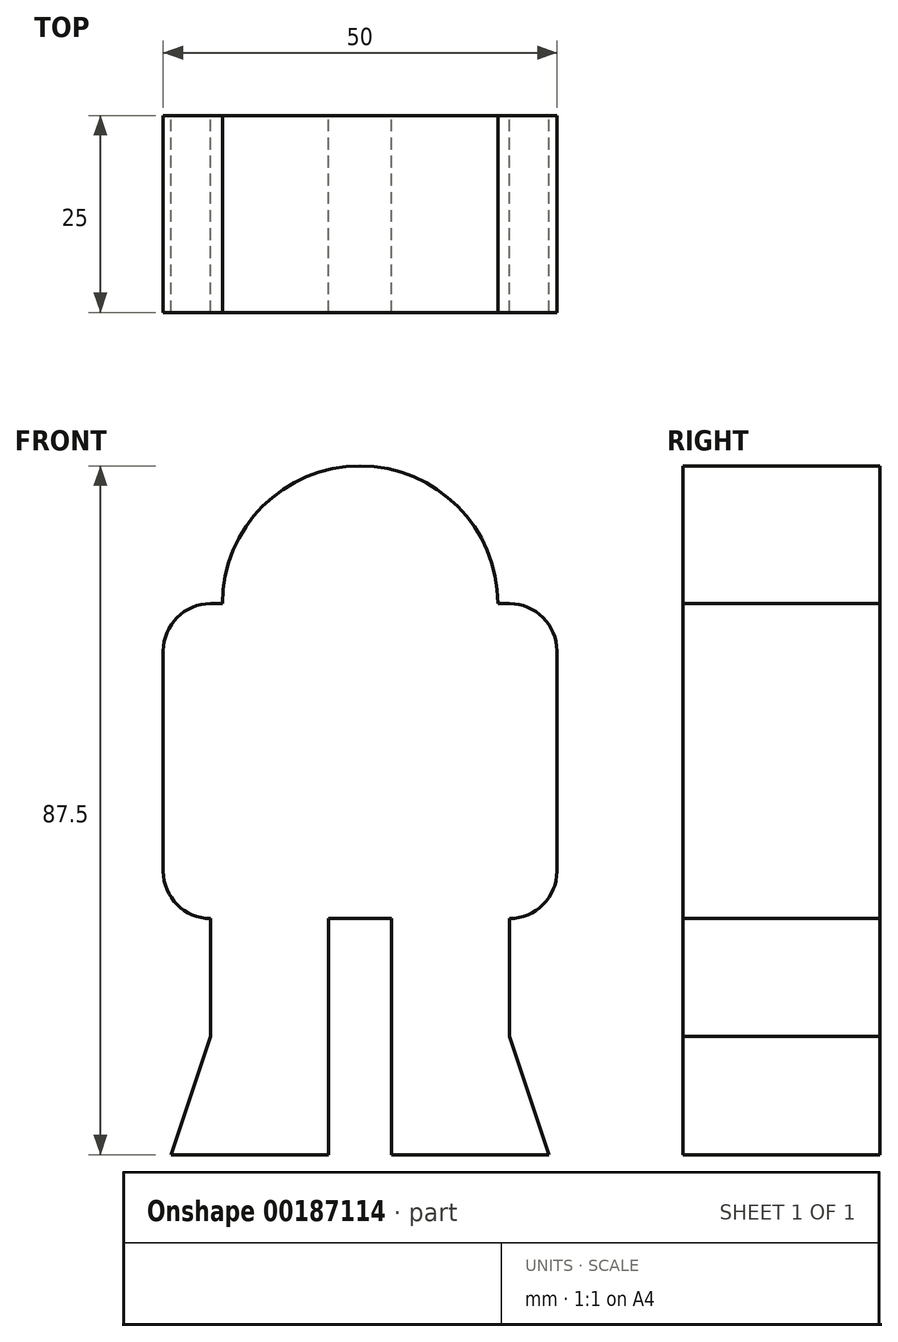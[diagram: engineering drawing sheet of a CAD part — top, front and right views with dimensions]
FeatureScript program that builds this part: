
annotation { "Feature Type Name" : "Feature", "Feature Type Description" : "" }
export const myFeature = defineFeature(function(context is Context, id is Id, definition is map)
    precondition{}
    {
        {
            var Q0;
            Q0=qCreatedBy(makeId("Front.planeOp"),FACE);
            var sketch = newSketch(context, id + "F0", { "sketchPlane" : qUnion([Q0])});
            skLineSegment(sketch, "E0.bottom", {"start": v(-19, -15) * mm, "end": v(19, -15) * mm});
            skLineSegment(sketch, "E0.top", {"start": v(-19, 25) * mm, "end": v(19, 25) * mm});
            skLineSegment(sketch, "E0.left", {"start": v(-25, -9) * mm, "end": v(-25, 19) * mm});
            skLineSegment(sketch, "E0.right", {"start": v(25, -9) * mm, "end": v(25, 19) * mm});
            skCircle(sketch, "E1", {"center": v(0, 25) * mm, "radius": 17.5 * mm});
            skPoint(sketch, "E2.visualSharp", {"position": v(-25, 25) * mm});
            skArc(sketch, "E2.filletArc", {"start": v(-19, 25) * mm, "mid": v(-23.24, 23.24) * mm, "end": v(-25, 19) * mm});
            skPoint(sketch, "E3.visualSharp", {"position": v(-25, -15) * mm});
            skArc(sketch, "E3.filletArc", {"start": v(-25, -9) * mm, "mid": v(-23.24, -13.24) * mm, "end": v(-19, -15) * mm});
            skPoint(sketch, "E4.visualSharp", {"position": v(25, -15) * mm});
            skArc(sketch, "E4.filletArc", {"start": v(19, -15) * mm, "mid": v(23.24, -13.24) * mm, "end": v(25, -9) * mm});
            skPoint(sketch, "E5.visualSharp", {"position": v(25, 25) * mm});
            skArc(sketch, "E5.filletArc", {"start": v(25, 19) * mm, "mid": v(23.24, 23.24) * mm, "end": v(19, 25) * mm});
            skLineSegment(sketch, "E6.bottom", {"start": v(-19, -15) * mm, "end": v(-4, -15) * mm});
            skLineSegment(sketch, "E6.top", {"start": v(-19, -45) * mm, "end": v(-4, -45) * mm});
            skLineSegment(sketch, "E6.left", {"start": v(-19, -15) * mm, "end": v(-19, -45) * mm});
            skLineSegment(sketch, "E6.right", {"start": v(-4, -15) * mm, "end": v(-4, -45) * mm});
            skLineSegment(sketch, "E7.bottom", {"start": v(19, -15) * mm, "end": v(4, -15) * mm});
            skLineSegment(sketch, "E7.top", {"start": v(19, -45) * mm, "end": v(4, -45) * mm});
            skLineSegment(sketch, "E7.left", {"start": v(19, -15) * mm, "end": v(19, -45) * mm});
            skLineSegment(sketch, "E7.right", {"start": v(4, -15) * mm, "end": v(4, -45) * mm});
            skLineSegment(sketch, "E8", {"start": v(-19, -45) * mm, "end": v(-24, -45) * mm});
            skLineSegment(sketch, "E9", {"start": v(-24, -45) * mm, "end": v(-19, -30) * mm});
            skLineSegment(sketch, "E10", {"start": v(19, -45) * mm, "end": v(24, -45) * mm});
            skLineSegment(sketch, "E11", {"start": v(24, -45) * mm, "end": v(19, -30) * mm});
            skSolve(sketch);
        }
        {
            var Q0;
            Q0 = qSketchRegion(id + "F0", true);
            extrude(context, id + "F1", {"entities" : qUnion([Q0]), "depth" : 25 * mm});
        }
    });
